# Revit family: Pressure_Balance_Rough_Valve-GROHE-35113000
name_source: partatom
category: Plumbing Fixtures
revit_build: Autodesk Revit 2016 (Build: 20150714_1515(x64)
units: mm (PartAtom-declared; Revit-internal decimal feet)

## family parameters
Cut with Voids When Loaded = Yes
Host = Face
OmniClass Number = 23.45.05.14.17
OmniClass Title = Showers
Part Type = Normal
Room Calculation Point = No
Round Connector Dimension = Use Diameter
Shared = Yes

## types (1)
- GROHSAFE 3.0 - 35113000 1/2" Stub-out  Inlet/Outlet
    Assembly Code = D2020300
    CW Connection = Yes
    CWFU = 3
    Connection CW Inlet Description = 1/2” Stub-out Connection Inlet
    Connection HW Inlet Description = 1/2” Stub-out Connection Inlet
    Connection Outlet Description = 1/2" Stub-out Connection Outlet
    Connection Size = 1/2"
    Default Elevation = 0"
    Dept From Wall Face To COFC = 1"
    Dept From Wall Face To Outlet = 2"
    Description = Pressure Balance Valve Rough with Stub-Outs for Press-Fit Connect with Service Stops
    Finish = DZR_Brass-Grohe
    HW Connection = Yes
    HWFU = 3
    Hot Inlet To Cold Inlet Width = 5 7/8"
    Inlet To Center = 2 15/16"
    Inlet to Wall = 1"
    Installation Type = Wall Mounted
    Manufacturer = Grohe
    Material = DZR_Brass-Grohe
    Model = 35113000
    Outlet To Center = 1 13/16"
    Outlet to Outlet = 4 3/4"
    Outlet to Wall = 2"
    Plaster Guard = Yes
    Price = Prices may vary. Please consult Manufacturer Representative for most up-to-date price list.
    ScrewDriver Stop = Yes
    Shower Outlet To Spout Outlet Width = 3 5/8"
    Specification = 1/2in Stub-out inlets/outlets; Includes plug for 3-port installation; Universal connection is 1/2” male threads by copper sweat; Flush plug included; Can be tested using flush plug with air (200 psi) or water 300 psi; Made of DZR Brass; Service stops; Cartridge ships with the trim
    URL = www.grohe.ca
    Vent Connection = No
    WFU = 4
    Waste Connection = No
    Water Connection Diameter = 1/2"

## geometry (parser evidence)
native form markers: Sweep x2
no freeform markers — native parametric forms only
